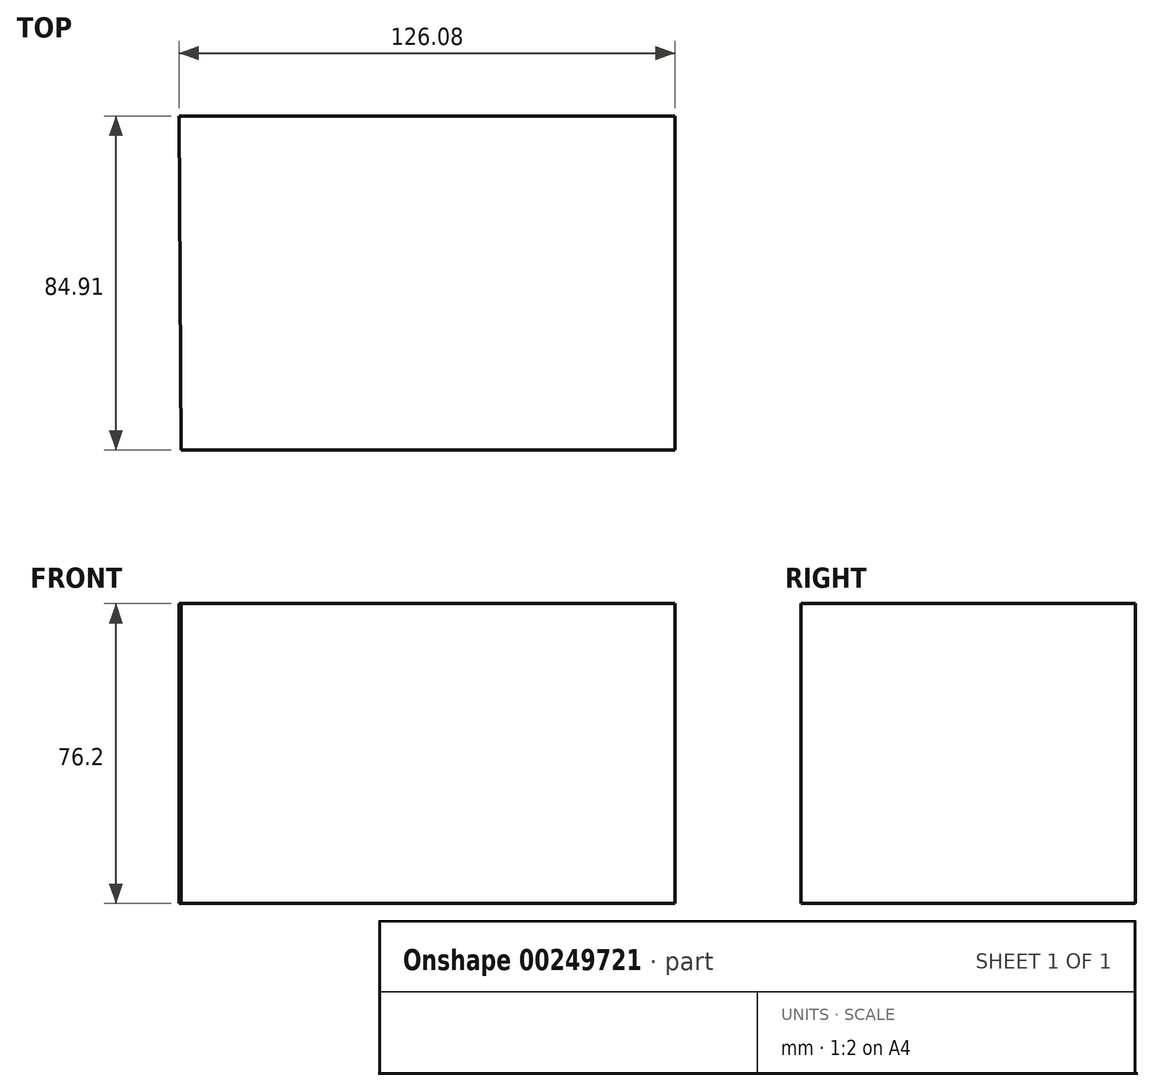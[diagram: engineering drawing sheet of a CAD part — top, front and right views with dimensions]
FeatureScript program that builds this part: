
annotation { "Feature Type Name" : "Feature", "Feature Type Description" : "" }
export const myFeature = defineFeature(function(context is Context, id is Id, definition is map)
    precondition{}
    {
        {
            var Q0;
            Q0=qCreatedBy(makeId("Top.planeOp"),FACE);
            var sketch = newSketch(context, id + "F0", { "sketchPlane" : qUnion([Q0])});
            skLineSegment(sketch, "E0", {"start": v(-125.48, 0) * mm, "end": v(0, 0) * mm});
            skLineSegment(sketch, "E1", {"start": v(0, 0) * mm, "end": v(0, 84.91) * mm});
            skLineSegment(sketch, "E2", {"start": v(0, 84.91) * mm, "end": v(-126.08, 84.91) * mm});
            skLineSegment(sketch, "E3", {"start": v(-126.08, 84.91) * mm, "end": v(-125.48, 0) * mm});
            skSolve(sketch);
        }
        {
            var Q0;
            Q0 = qSketchRegion(id + "F0", true);
            extrude(context, id + "F1", {"entities" : qUnion([Q0]), "depth" : 76.2 * mm});
        }
    });
